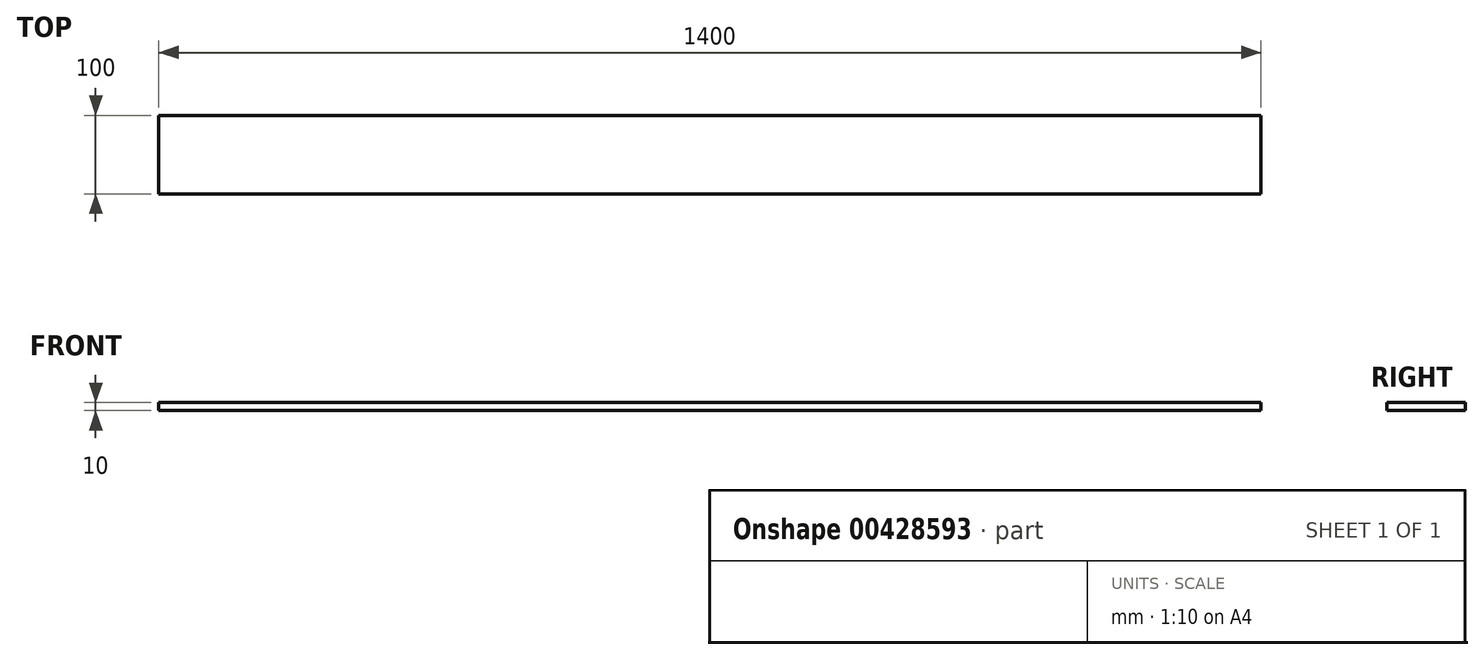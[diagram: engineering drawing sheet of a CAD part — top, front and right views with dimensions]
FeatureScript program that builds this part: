
annotation { "Feature Type Name" : "Feature", "Feature Type Description" : "" }
export const myFeature = defineFeature(function(context is Context, id is Id, definition is map)
    precondition{}
    {
        {
            var Q0;
            Q0=qCreatedBy(makeId("Top.planeOp"),FACE);
            var sketch = newSketch(context, id + "F0", { "sketchPlane" : qUnion([Q0])});
            skLineSegment(sketch, "E0.bottom", {"start": v(0, 0) * mm, "end": v(1400, 0) * mm});
            skLineSegment(sketch, "E0.top", {"start": v(0, 100) * mm, "end": v(1400, 100) * mm});
            skLineSegment(sketch, "E0.left", {"start": v(0, 0) * mm, "end": v(0, 100) * mm});
            skLineSegment(sketch, "E0.right", {"start": v(1400, 0) * mm, "end": v(1400, 100) * mm});
            skSolve(sketch);
        }
        {
            var Q0;
            Q0=makeQuery(id+"F0.imprint","IMPRINT",FACE,{"disambiguationData":[TD([[makeQuery(id+"F0.imprint","IMPRINT",EDGE,{"derivedFrom":sQuery(id+"F0.wireOp",EDGE,"E0.bottom")}),1.0]])]});
            extrude(context, id + "F1", {"entities" : qUnion([Q0]), "depth" : 10 * mm});
        }
    });
